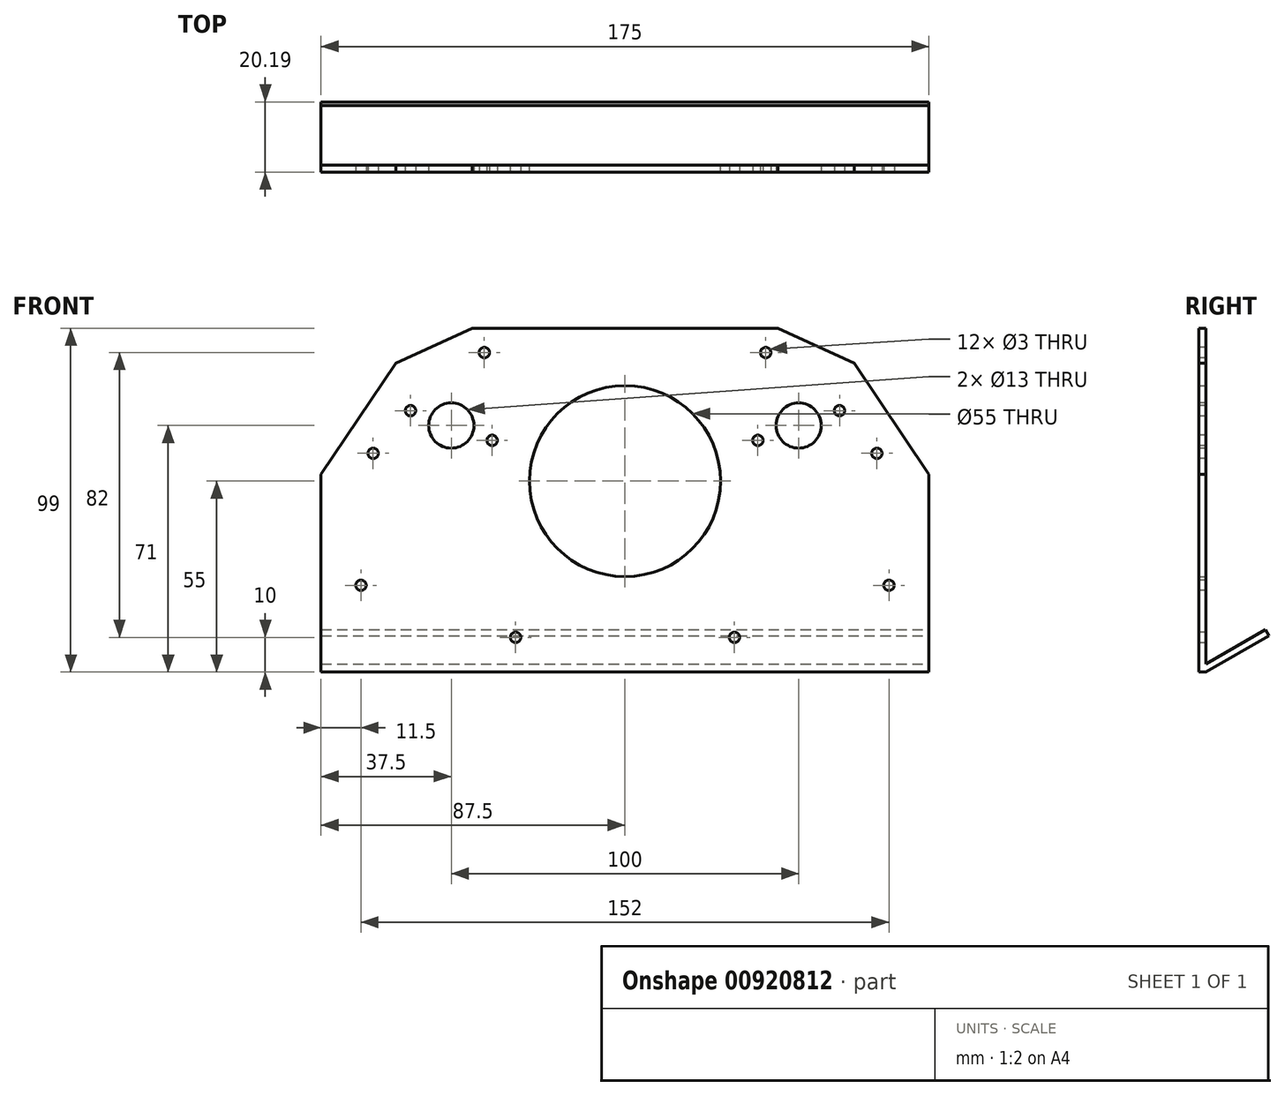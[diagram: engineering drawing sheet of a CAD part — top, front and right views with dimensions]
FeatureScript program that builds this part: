
annotation { "Feature Type Name" : "Feature", "Feature Type Description" : "" }
export const myFeature = defineFeature(function(context is Context, id is Id, definition is map)
    precondition{}
    {
        {
            var Q0;
            Q0=qCreatedBy(makeId("Front.planeOp"),FACE);
            var sketch = newSketch(context, id + "F0", { "sketchPlane" : qUnion([Q0])});
            skCircle(sketch, "E0", {"center": v(0, 0) * mm, "radius": 27.5 * mm});
            skLineSegment(sketch, "E1", {"start": v(-44, 44) * mm, "end": v(44, 44) * mm});
            skLineSegment(sketch, "E2", {"start": v(-87.5, 2) * mm, "end": v(-87.5, -55) * mm});
            skLineSegment(sketch, "E3", {"start": v(-87.5, 2) * mm, "end": v(-66, 34) * mm});
            skLineSegment(sketch, "E4", {"start": v(-66, 34) * mm, "end": v(-44, 44) * mm});
            skLineSegment(sketch, "E5", {"start": v(-87.5, -55) * mm, "end": v(87.5, -55) * mm});
            skLineSegment(sketch, "E6", {"start": v(87.5, -55) * mm, "end": v(87.5, 2) * mm});
            skLineSegment(sketch, "E7", {"start": v(87.5, 2) * mm, "end": v(66, 34) * mm});
            skLineSegment(sketch, "E8", {"start": v(66, 34) * mm, "end": v(44, 44) * mm});
            skSolve(sketch);
        }
        {
            var Q0;
            Q0 = qSketchRegion(id + "F0", true);
            extrude(context, id + "F1", {"entities" : qUnion([Q0]), "depth" : 2 * mm, "offsetDistance" : 25 * mm});
        }
        {
            var Q0;
            Q0=makeQuery(id+"F1.opExtrude","CAP_FACE",FACE,{"disambiguationData":[OSD([sQuery(id+"F0.wireOp",EDGE,"E0"),sQuery(id+"F0.wireOp",EDGE,"E1"),sQuery(id+"F0.wireOp",EDGE,"E2"),sQuery(id+"F0.wireOp",EDGE,"E3"),sQuery(id+"F0.wireOp",EDGE,"E4"),sQuery(id+"F0.wireOp",EDGE,"E5"),sQuery(id+"F0.wireOp",EDGE,"E6"),sQuery(id+"F0.wireOp",EDGE,"E7"),sQuery(id+"F0.wireOp",EDGE,"E8")])],"isStart":false});
            var sketch = newSketch(context, id + "F2", { "sketchPlane" : qUnion([Q0])});
            skCircle(sketch, "E9", {"center": v(50, 16) * mm, "radius": 6.5 * mm});
            skCircle(sketch, "E10", {"center": v(61.75, 20.28) * mm, "radius": 1.5 * mm});
            skCircle(sketch, "E11", {"center": v(38.25, 11.72) * mm, "radius": 1.5 * mm});
            skLineSegment(sketch, "E12", {"start": v(50, 16) * mm, "end": v(39.8, 44) * mm, "construction": true});
            skLineSegment(sketch, "E13", {"start": v(38.25, 11.72) * mm, "end": v(61.75, 20.28) * mm, "construction": true});
            skCircle(sketch, "E14.MirrorC", {"center": v(-38.25, 11.72) * mm, "radius": 1.5 * mm});
            skCircle(sketch, "E15.MirrorC", {"center": v(-61.75, 20.28) * mm, "radius": 1.5 * mm});
            skLineSegment(sketch, "E16.MirrorCS", {"start": v(-38.25, 11.72) * mm, "end": v(-61.75, 20.28) * mm, "construction": true});
            skCircle(sketch, "E17.MirrorC", {"center": v(-50, 16) * mm, "radius": 6.5 * mm});
            skLineSegment(sketch, "E18.MirrorCS", {"start": v(-50, 16) * mm, "end": v(-39.8, 44) * mm, "construction": true});
            skSolve(sketch);
        }
        {
            var Q0;
            Q0 = qSketchRegion(id + "F2", true);
            extrude(context, id + "F3", {"entities" : qUnion([Q0]), "operationType" : NewBodyOperationType.REMOVE, "endBound" : BoundingType.UP_TO_NEXT, "oppositeDirection" : true, "depth" : 25 * mm, "offsetDistance" : 25 * mm});
        }
        {
            var Q0;
            Q0=makeQuery(id+"F1.opExtrude","CAP_FACE",FACE,{"disambiguationData":[OSD([sQuery(id+"F0.wireOp",EDGE,"E0"),sQuery(id+"F0.wireOp",EDGE,"E1"),sQuery(id+"F0.wireOp",EDGE,"E2"),sQuery(id+"F0.wireOp",EDGE,"E3"),sQuery(id+"F0.wireOp",EDGE,"E4"),sQuery(id+"F0.wireOp",EDGE,"E5"),sQuery(id+"F0.wireOp",EDGE,"E6"),sQuery(id+"F0.wireOp",EDGE,"E7"),sQuery(id+"F0.wireOp",EDGE,"E8")])],"isStart":false});
            var sketch = newSketch(context, id + "F4", { "sketchPlane" : qUnion([Q0])});
            skCircle(sketch, "E19", {"center": v(-31.5, -45) * mm, "radius": 1.5 * mm});
            skCircle(sketch, "E20", {"center": v(31.5, -45) * mm, "radius": 1.5 * mm});
            skCircle(sketch, "E21", {"center": v(76, -30) * mm, "radius": 1.5 * mm});
            skCircle(sketch, "E22", {"center": v(72.5, 8) * mm, "radius": 1.5 * mm});
            skCircle(sketch, "E23", {"center": v(40.5, 37) * mm, "radius": 1.5 * mm});
            skCircle(sketch, "E24.MirrorC", {"center": v(-40.5, 37) * mm, "radius": 1.5 * mm});
            skCircle(sketch, "E25.MirrorC", {"center": v(-76, -30) * mm, "radius": 1.5 * mm});
            skCircle(sketch, "E26.MirrorC", {"center": v(-72.5, 8) * mm, "radius": 1.5 * mm});
            skSolve(sketch);
        }
        {
            var Q0;
            Q0 = qSketchRegion(id + "F4", true);
            extrude(context, id + "F5", {"entities" : qUnion([Q0]), "operationType" : NewBodyOperationType.REMOVE, "endBound" : BoundingType.UP_TO_NEXT, "oppositeDirection" : true, "depth" : 25 * mm, "offsetDistance" : 25 * mm});
        }
        {
            var Q0;
            Q0=makeQuery(id+"F1.opExtrude","SWEPT_FACE",FACE,{"disambiguationData":[OSD([sQuery(id+"F0.wireOp",EDGE,"E6")])]});
            var sketch = newSketch(context, id + "F6", { "sketchPlane" : qUnion([Q0])});
            skLineSegment(sketch, "E27", {"start": v(0, -55) * mm, "end": v(18.19, -44.5) * mm});
            skLineSegment(sketch, "E28", {"start": v(18.19, -44.5) * mm, "end": v(17.19, -42.77) * mm});
            skLineSegment(sketch, "E29", {"start": v(17.19, -42.77) * mm, "end": v(0, -52.7) * mm});
            skLineSegment(sketch, "E30", {"start": v(0, -52.7) * mm, "end": v(0, -55) * mm});
            skSolve(sketch);
        }
        {
            var Q0;
            Q0 = qSketchRegion(id + "F6", true);
            var Q1;
            Q1=makeQuery(id+"F1.opExtrude","SWEPT_FACE",FACE,{"disambiguationData":[OSD([sQuery(id+"F0.wireOp",EDGE,"E2")])]});
            extrude(context, id + "F7", {"entities" : qUnion([Q0]), "operationType" : NewBodyOperationType.ADD, "endBound" : BoundingType.UP_TO_SURFACE, "oppositeDirection" : true, "depth" : 25 * mm, "endBoundEntityFace" : qUnion([Q1]), "offsetDistance" : 25 * mm});
        }
    });
